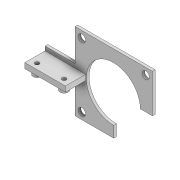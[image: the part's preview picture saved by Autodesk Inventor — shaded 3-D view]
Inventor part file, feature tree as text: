
AUTODESK INVENTOR PART (.ipt)
format: ipt  version: 2022 (Build 260153000, 153)  size: 151,040 bytes
history: native  units: mm
features: extrude x5, sketch x5, projected_geometry x2
ambient origin geometry x8: Origin, YZ Plane, XZ Plane, XY Plane, X Axis, Y Axis, Z Axis, Center Point
bodies: Solid1 (feature_tree)
feature tree (12):
  extrude  "Extrusion1"  Depth=57.2mm
  extrude  "Extrusion5"  Depth=10.0mm
  extrude  "Extrusion6"  Depth=30.0mm
  extrude  "Extrusion7"  Depth=30.0mm
  extrude  "Extrusion8"  Depth=15.0mm TaperAngle=0.0deg
  sketch  "Sketch1"  dims[d0=2.0mm d1=57.2mm]
  sketch  "Sketch6"  dims[d2=2.0mm d3=0.0mm d14=10.0mm]
  sketch  "Sketch7"  dims[d15=2.0mm d16=0.0mm d17=30.0mm]
  sketch  "Sketch8"  dims[d18=2.0mm d19=30.0mm]
  sketch  "Sketch9"  dims[d20=4.0mm d21=15.0mm d22=0.0mm d23=3.0mm d24=0.0mm d25=0.0mm d26=0.0mm d4=0.5mm d5=0.872665mm d6=0.5mm d7=0.872665mm]
  projected_geometry  "Projected Loop3"
  projected_geometry  "Projected Loop4"
